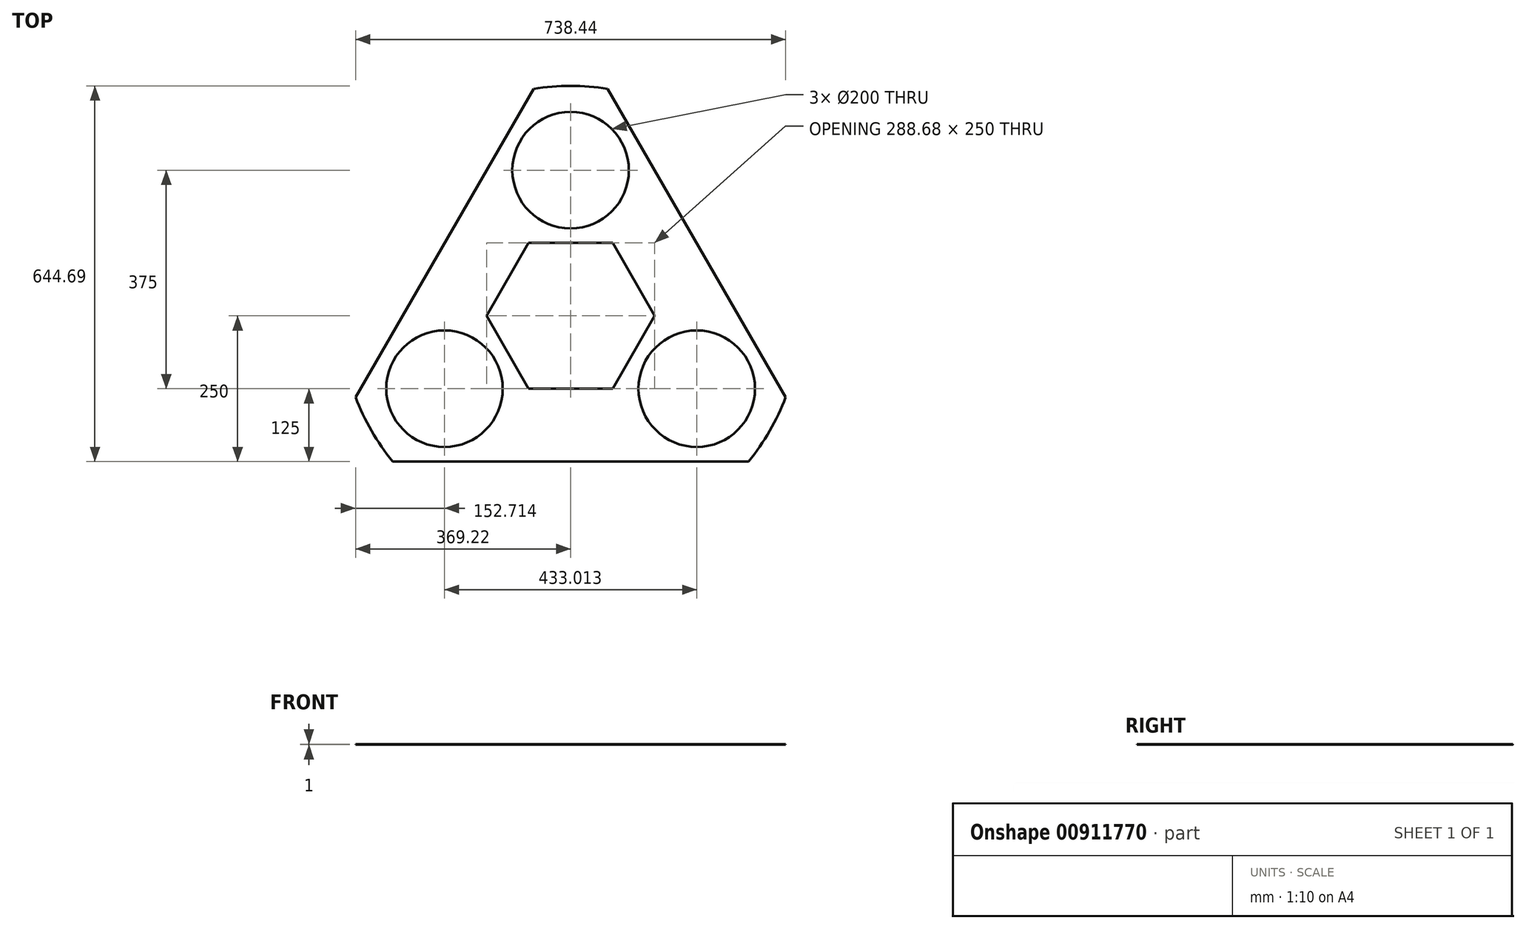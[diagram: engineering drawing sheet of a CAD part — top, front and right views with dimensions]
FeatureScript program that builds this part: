
annotation { "Feature Type Name" : "Feature", "Feature Type Description" : "" }
export const myFeature = defineFeature(function(context is Context, id is Id, definition is map)
    precondition{}
    {
        {
            var Q0;
            Q0=qCreatedBy(makeId("Top.planeOp"),FACE);
            var sketch = newSketch(context, id + "F0", { "sketchPlane" : qUnion([Q0])});
            skLineSegment(sketch, "E0", {"start": v(-433.01, -250) * mm, "end": v(0, 500) * mm});
            skLineSegment(sketch, "E1", {"start": v(0, 500) * mm, "end": v(433.01, -250) * mm});
            skLineSegment(sketch, "E2", {"start": v(433.01, -250) * mm, "end": v(-433.01, -250) * mm});
            skCircle(sketch, "E3", {"center": v(0, 0) * mm, "radius": 250 * mm});
            skLineSegment(sketch, "E4", {"start": v(-216.5, -125) * mm, "end": v(0, 250) * mm});
            skLineSegment(sketch, "E5", {"start": v(0, 250) * mm, "end": v(216.5, -125) * mm});
            skLineSegment(sketch, "E6", {"start": v(216.5, -125) * mm, "end": v(-216.5, -125) * mm});
            skCircle(sketch, "E7", {"center": v(0, 250) * mm, "radius": 100 * mm});
            skCircle(sketch, "E8", {"center": v(-216.5, -125) * mm, "radius": 100 * mm});
            skCircle(sketch, "E9", {"center": v(216.5, -125) * mm, "radius": 100 * mm});
            skCircle(sketch, "E10", {"center": v(0, 0) * mm, "radius": 394.69 * mm});
            skLineSegment(sketch, "E11", {"start": v(-216.5, 125) * mm, "end": v(0, -250) * mm});
            skLineSegment(sketch, "E12", {"start": v(0, -250) * mm, "end": v(216.5, 125) * mm});
            skLineSegment(sketch, "E13", {"start": v(216.5, 125) * mm, "end": v(-216.5, 125) * mm});
            skPoint(sketch, "E14", {"position": v(0, 350) * mm});
            skPoint(sketch, "E15", {"position": v(-214.12, -224.97) * mm});
            skPoint(sketch, "E16", {"position": v(-116.5, -125) * mm});
            skPoint(sketch, "E17", {"position": v(116.5, -125) * mm});
            skSolve(sketch);
        }
        {
            var Q0;
            {var subQ0=sQuery(id+"F0.wireOp",EDGE,"E13");var subQ5=sQuery(id+"F0.wireOp",EDGE,"E4");var subQ6=makeQuery(id+"F0.imprint","INTERSECT",VERTEX,{"derivedFrom":[subQ5,subQ0]});Q0=makeQuery(id+"F0.imprint","IMPRINT",FACE,{"disambiguationData":[TD([[makeQuery(id+"F0.imprint","IMPRINT",EDGE,{"disambiguationData":[TD([[subQ6,-1.0]])],"derivedFrom":subQ5}),1.0]])]});}
            var Q1;
            {var subQ0=sQuery(id+"F0.wireOp",EDGE,"E13");var subQ1=sQuery(id+"F0.wireOp",EDGE,"E4");var subQ2=makeQuery(id+"F0.imprint","INTERSECT",VERTEX,{"derivedFrom":[subQ1,subQ0]});Q1=makeQuery(id+"F0.imprint","IMPRINT",FACE,{"disambiguationData":[TD([[makeQuery(id+"F0.imprint","IMPRINT",EDGE,{"disambiguationData":[TD([[subQ2,-1.0]])],"derivedFrom":subQ1}),-1.0]])]});}
            var Q2;
            {var subQ3=sQuery(id+"F0.wireOp",EDGE,"E7");var subQ5=sQuery(id+"F0.wireOp",EDGE,"E5");var subQ6=makeQuery(id+"F0.imprint","INTERSECT",VERTEX,{"derivedFrom":[subQ5,subQ3]});Q2=makeQuery(id+"F0.imprint","IMPRINT",FACE,{"disambiguationData":[TD([[makeQuery(id+"F0.imprint","IMPRINT",EDGE,{"disambiguationData":[TD([[subQ6,-1.0]])],"derivedFrom":subQ5}),1.0]])]});}
            var Q3;
            {var subQ0=sQuery(id+"F0.wireOp",EDGE,"E13");var subQ1=sQuery(id+"F0.wireOp",EDGE,"E5");var subQ2=makeQuery(id+"F0.imprint","INTERSECT",VERTEX,{"derivedFrom":[subQ1,subQ0]});Q3=makeQuery(id+"F0.imprint","IMPRINT",FACE,{"disambiguationData":[TD([[makeQuery(id+"F0.imprint","IMPRINT",EDGE,{"disambiguationData":[TD([[subQ2,-1.0]])],"derivedFrom":subQ1}),1.0]])]});}
            var Q4;
            {var subQ0=sQuery(id+"F0.wireOp",EDGE,"E12");var subQ5=sQuery(id+"F0.wireOp",EDGE,"E5");var subQ6=makeQuery(id+"F0.imprint","INTERSECT",VERTEX,{"derivedFrom":[subQ5,subQ0]});Q4=makeQuery(id+"F0.imprint","IMPRINT",FACE,{"disambiguationData":[TD([[makeQuery(id+"F0.imprint","IMPRINT",EDGE,{"disambiguationData":[TD([[subQ6,-1.0]])],"derivedFrom":subQ5}),1.0]])]});}
            var Q5;
            {var subQ0=sQuery(id+"F0.wireOp",EDGE,"E12");var subQ1=sQuery(id+"F0.wireOp",EDGE,"E5");var subQ2=makeQuery(id+"F0.imprint","INTERSECT",VERTEX,{"derivedFrom":[subQ1,subQ0]});Q5=makeQuery(id+"F0.imprint","IMPRINT",FACE,{"disambiguationData":[TD([[makeQuery(id+"F0.imprint","IMPRINT",EDGE,{"disambiguationData":[TD([[subQ2,-1.0]])],"derivedFrom":subQ1}),-1.0]])]});}
            var Q6;
            {var subQ3=sQuery(id+"F0.wireOp",EDGE,"E9");var subQ5=sQuery(id+"F0.wireOp",EDGE,"E6");var subQ6=makeQuery(id+"F0.imprint","INTERSECT",VERTEX,{"derivedFrom":[subQ5,subQ3]});Q6=makeQuery(id+"F0.imprint","IMPRINT",FACE,{"disambiguationData":[TD([[makeQuery(id+"F0.imprint","IMPRINT",EDGE,{"disambiguationData":[TD([[subQ6,-1.0]])],"derivedFrom":subQ5}),1.0]])]});}
            var Q7;
            {var subQ0=sQuery(id+"F0.wireOp",EDGE,"E12");var subQ1=sQuery(id+"F0.wireOp",EDGE,"E6");var subQ2=makeQuery(id+"F0.imprint","INTERSECT",VERTEX,{"derivedFrom":[subQ1,subQ0]});Q7=makeQuery(id+"F0.imprint","IMPRINT",FACE,{"disambiguationData":[TD([[makeQuery(id+"F0.imprint","IMPRINT",EDGE,{"disambiguationData":[TD([[subQ2,-1.0]])],"derivedFrom":subQ1}),1.0]])]});}
            var Q8;
            {var subQ0=sQuery(id+"F0.wireOp",EDGE,"E11");var subQ5=sQuery(id+"F0.wireOp",EDGE,"E6");var subQ6=makeQuery(id+"F0.imprint","INTERSECT",VERTEX,{"derivedFrom":[subQ5,subQ0]});Q8=makeQuery(id+"F0.imprint","IMPRINT",FACE,{"disambiguationData":[TD([[makeQuery(id+"F0.imprint","IMPRINT",EDGE,{"disambiguationData":[TD([[subQ6,-1.0]])],"derivedFrom":subQ5}),1.0]])]});}
            var Q9;
            {var subQ0=sQuery(id+"F0.wireOp",EDGE,"E8");var subQ1=sQuery(id+"F0.wireOp",EDGE,"E4");var subQ2=makeQuery(id+"F0.imprint","INTERSECT",VERTEX,{"derivedFrom":[subQ1,subQ0]});Q9=makeQuery(id+"F0.imprint","IMPRINT",FACE,{"disambiguationData":[TD([[makeQuery(id+"F0.imprint","IMPRINT",EDGE,{"disambiguationData":[TD([[subQ2,-1.0]])],"derivedFrom":subQ1}),-1.0]])]});}
            var Q10;
            {var subQ3=sQuery(id+"F0.wireOp",EDGE,"E8");var subQ5=sQuery(id+"F0.wireOp",EDGE,"E4");var subQ6=makeQuery(id+"F0.imprint","INTERSECT",VERTEX,{"derivedFrom":[subQ5,subQ3]});Q10=makeQuery(id+"F0.imprint","IMPRINT",FACE,{"disambiguationData":[TD([[makeQuery(id+"F0.imprint","IMPRINT",EDGE,{"disambiguationData":[TD([[subQ6,-1.0]])],"derivedFrom":subQ5}),1.0]])]});}
            var Q11;
            {var subQ1=sQuery(id+"F0.wireOp",EDGE,"E3");var subQ4=sQuery(id+"F0.wireOp",EDGE,"E7");var subQ10=makeQuery(id+"F0.imprint","INTERSECT",VERTEX,{"disambiguationData":[OD(0.0)],"derivedFrom":[subQ1,subQ4]});Q11=makeQuery(id+"F0.imprint","IMPRINT",FACE,{"disambiguationData":[TD([[makeQuery(id+"F0.imprint","IMPRINT",EDGE,{"disambiguationData":[TD([[subQ10,-1.0]])],"derivedFrom":subQ4}),-1.0]])]});}
            var Q12;
            {var subQ1=sQuery(id+"F0.wireOp",EDGE,"E3");var subQ4=sQuery(id+"F0.wireOp",EDGE,"E9");var subQ8=makeQuery(id+"F0.imprint","INTERSECT",VERTEX,{"disambiguationData":[OD(0.0)],"derivedFrom":[subQ1,subQ4]});Q12=makeQuery(id+"F0.imprint","IMPRINT",FACE,{"disambiguationData":[TD([[makeQuery(id+"F0.imprint","IMPRINT",EDGE,{"disambiguationData":[TD([[subQ8,-1.0]])],"derivedFrom":subQ4}),-1.0]])]});}
            var Q13;
            {var subQ1=sQuery(id+"F0.wireOp",EDGE,"E3");var subQ4=sQuery(id+"F0.wireOp",EDGE,"E8");var subQ10=makeQuery(id+"F0.imprint","INTERSECT",VERTEX,{"disambiguationData":[OD(0.0)],"derivedFrom":[subQ1,subQ4]});Q13=makeQuery(id+"F0.imprint","IMPRINT",FACE,{"disambiguationData":[TD([[makeQuery(id+"F0.imprint","IMPRINT",EDGE,{"disambiguationData":[TD([[subQ10,-1.0]])],"derivedFrom":subQ4}),-1.0]])]});}
            var Q14;
            {var subQ0=sQuery(id+"F0.wireOp",EDGE,"E11");var subQ1=sQuery(id+"F0.wireOp",EDGE,"E4");var subQ2=makeQuery(id+"F0.imprint","INTERSECT",VERTEX,{"derivedFrom":[subQ1,subQ0]});Q14=makeQuery(id+"F0.imprint","IMPRINT",FACE,{"disambiguationData":[TD([[makeQuery(id+"F0.imprint","IMPRINT",EDGE,{"disambiguationData":[TD([[subQ2,-1.0]])],"derivedFrom":subQ1}),1.0]])]});}
            extrude(context, id + "F1", {"entities" : qUnion([Q0, Q1, Q2, Q3, Q4, Q5, Q6, Q7, Q8, Q9, Q10, Q11, Q12, Q13, Q14]), "depth" : 1 * mm, "offsetDistance" : 25 * mm});
        }
    });
